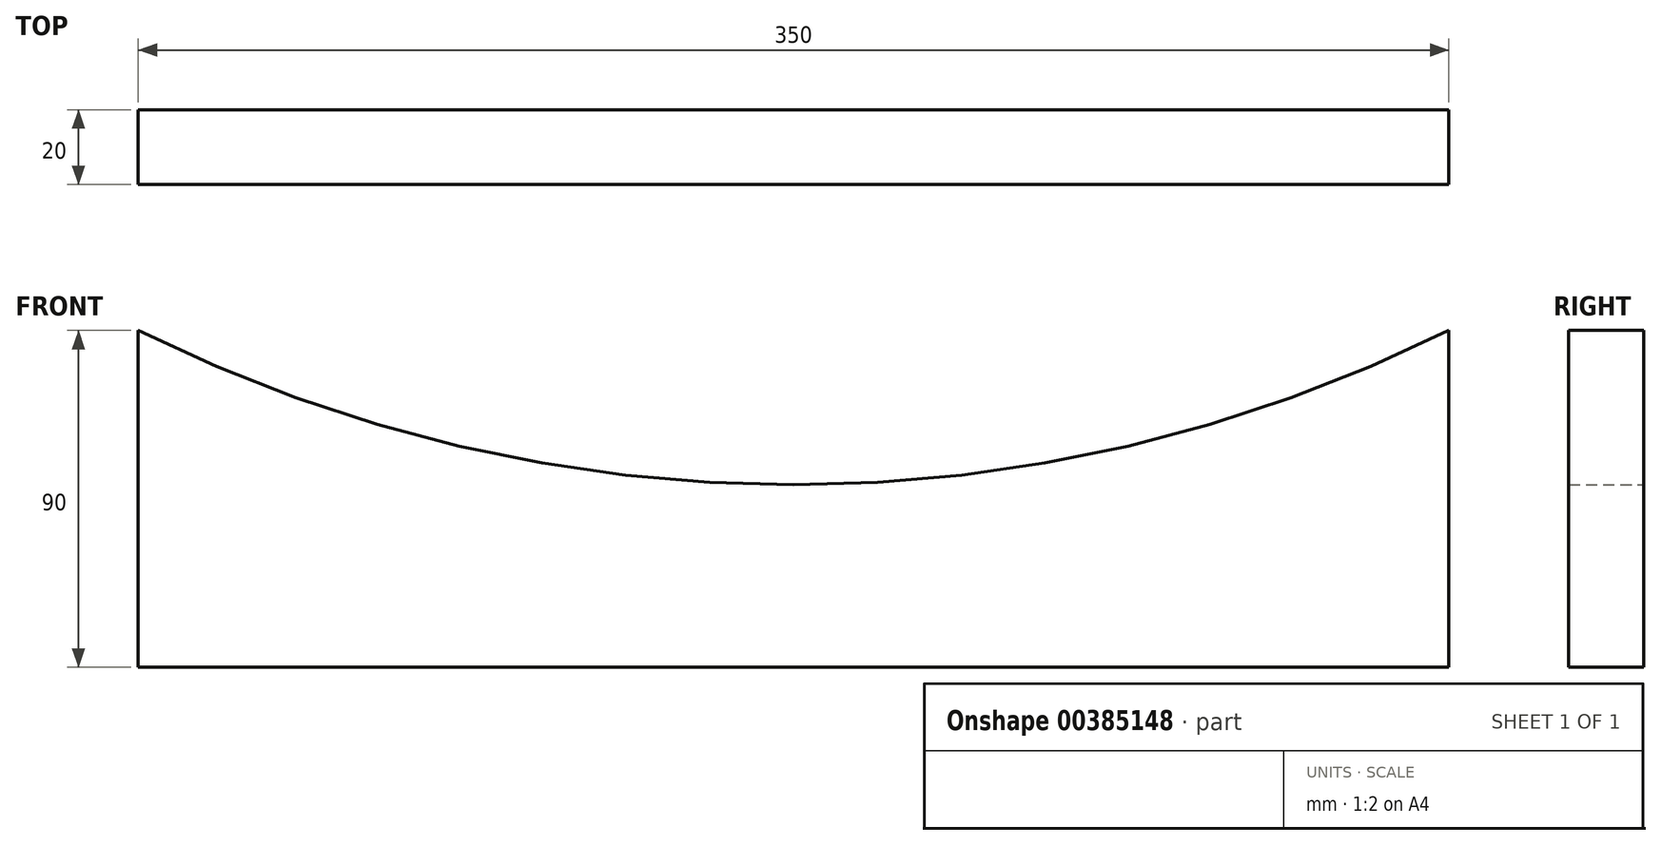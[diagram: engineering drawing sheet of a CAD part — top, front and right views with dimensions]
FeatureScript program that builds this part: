
annotation { "Feature Type Name" : "Feature", "Feature Type Description" : "" }
export const myFeature = defineFeature(function(context is Context, id is Id, definition is map)
    precondition{}
    {
        {
            var Q0;
            Q0=qCreatedBy(makeId("Front.planeOp"),FACE);
            var sketch = newSketch(context, id + "F0", { "sketchPlane" : qUnion([Q0])});
            skLineSegment(sketch, "E0", {"start": v(-175, 0) * mm, "end": v(175, 0) * mm});
            skLineSegment(sketch, "E1", {"start": v(175, 0) * mm, "end": v(175, 90) * mm});
            skLineSegment(sketch, "E2", {"start": v(-175, 0) * mm, "end": v(-175, 90) * mm});
            skArc(sketch, "E3", {"start": v(-175, 90) * mm, "mid": v(0, 48.8) * mm, "end": v(175, 90) * mm});
            skSolve(sketch);
        }
        {
            var Q0;
            Q0 = qSketchRegion(id + "F0", true);
            extrude(context, id + "F1", {"entities" : qUnion([Q0]), "depth" : 20 * mm});
        }
        {
            var Q0;
            Q0 = qSketchRegion(id + "F0", true);
            extrude(context, id + "F2", {"entities" : qUnion([Q0]), "operationType" : NewBodyOperationType.ADD, "depth" : 20 * mm});
        }
    });
